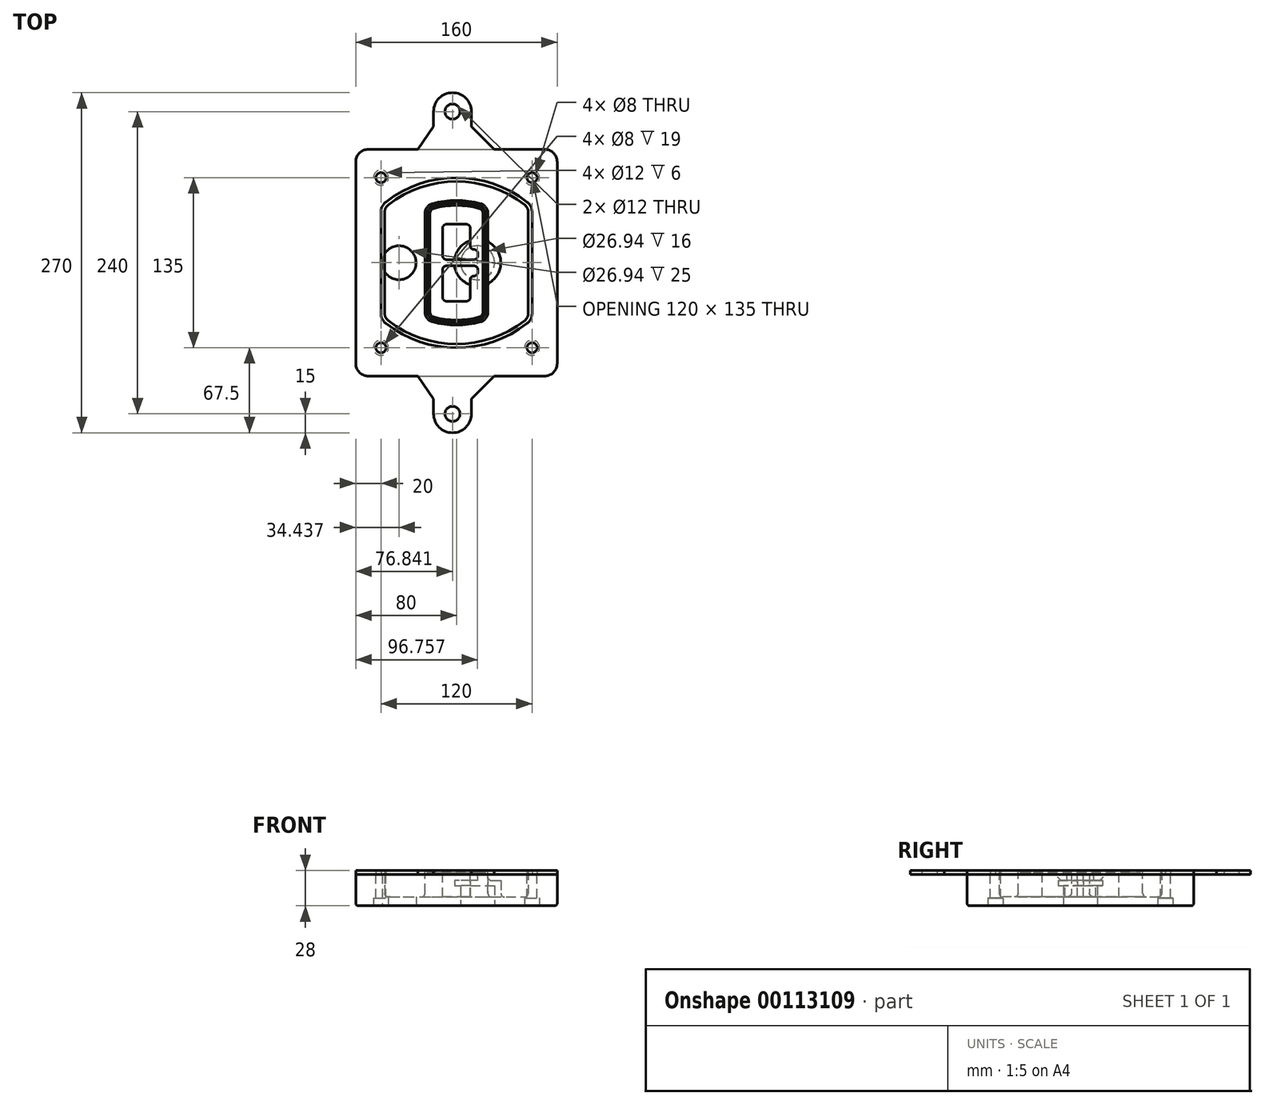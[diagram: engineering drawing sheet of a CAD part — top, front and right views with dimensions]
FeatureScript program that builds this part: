
annotation { "Feature Type Name" : "Feature", "Feature Type Description" : "" }
export const myFeature = defineFeature(function(context is Context, id is Id, definition is map)
    precondition{}
    {
        {
            var Q0;
            Q0=qCreatedBy(makeId("Top.planeOp"),FACE);
            var sketch = newSketch(context, id + "F0", { "sketchPlane" : qUnion([Q0])});
            skPoint(sketch, "E0.rect.middle", {"position": v(0, 0) * mm});
            skLineSegment(sketch, "E1.bottom", {"start": v(-70, -90) * mm, "end": v(70, -90) * mm});
            skLineSegment(sketch, "E1.top", {"start": v(-70, 90) * mm, "end": v(70, 90) * mm});
            skLineSegment(sketch, "E1.left", {"start": v(-80, -80) * mm, "end": v(-80, 80) * mm});
            skLineSegment(sketch, "E1.right", {"start": v(80, -80) * mm, "end": v(80, 80) * mm});
            skLineSegment(sketch, "E2", {"start": v(-80, 90) * mm, "end": v(80, -90) * mm, "construction": true});
            skLineSegment(sketch, "E3", {"start": v(80, 90) * mm, "end": v(-80, -90) * mm, "construction": true});
            skCircle(sketch, "E4", {"center": v(-60, 67.5) * mm, "radius": 4 * mm});
            skCircle(sketch, "E5", {"center": v(60, 67.5) * mm, "radius": 4 * mm});
            skCircle(sketch, "E6", {"center": v(60, -67.5) * mm, "radius": 4 * mm});
            skCircle(sketch, "E7", {"center": v(-60, -67.5) * mm, "radius": 4 * mm});
            skLineSegment(sketch, "E8", {"start": v(-60, 67.5) * mm, "end": v(60, 67.5) * mm, "construction": true});
            skLineSegment(sketch, "E9", {"start": v(60, 67.5) * mm, "end": v(60, -67.5) * mm, "construction": true});
            skLineSegment(sketch, "E10", {"start": v(60, -67.5) * mm, "end": v(-60, -67.5) * mm, "construction": true});
            skLineSegment(sketch, "E11", {"start": v(-60, -67.5) * mm, "end": v(-60, 67.5) * mm, "construction": true});
            skLineSegment(sketch, "E12", {"start": v(-60, 40.3) * mm, "end": v(-60, -40.3) * mm});
            skLineSegment(sketch, "E13", {"start": v(60, 40.3) * mm, "end": v(60, -40.3) * mm});
            skArc(sketch, "E14", {"start": v(56.15, 48.18) * mm, "mid": v(0, 67.5) * mm, "end": v(-56.15, 48.18) * mm});
            skArc(sketch, "E15", {"start": v(-56.15, -48.18) * mm, "mid": v(0, -67.5) * mm, "end": v(56.15, -48.18) * mm});
            skLineSegment(sketch, "E16", {"start": v(-60, 0) * mm, "end": v(60, 0) * mm, "construction": true});
            skPoint(sketch, "E17.visualSharp", {"position": v(-60, -45) * mm});
            skArc(sketch, "E17.filletArc", {"start": v(-60, -40.3) * mm, "mid": v(-58.99, -44.68) * mm, "end": v(-56.15, -48.18) * mm});
            skPoint(sketch, "E18.visualSharp", {"position": v(-60, 45) * mm});
            skArc(sketch, "E18.filletArc", {"start": v(-56.15, 48.18) * mm, "mid": v(-58.99, 44.68) * mm, "end": v(-60, 40.3) * mm});
            skPoint(sketch, "E19.visualSharp", {"position": v(60, 45) * mm});
            skArc(sketch, "E19.filletArc", {"start": v(60, 40.3) * mm, "mid": v(58.99, 44.68) * mm, "end": v(56.15, 48.18) * mm});
            skPoint(sketch, "E20.visualSharp", {"position": v(60, -45) * mm});
            skArc(sketch, "E20.filletArc", {"start": v(56.15, -48.18) * mm, "mid": v(58.99, -44.68) * mm, "end": v(60, -40.3) * mm});
            skPoint(sketch, "E21.visualSharp", {"position": v(-80, 90) * mm});
            skArc(sketch, "E21.filletArc", {"start": v(-70, 90) * mm, "mid": v(-77.07, 87.07) * mm, "end": v(-80, 80) * mm});
            skPoint(sketch, "E22.visualSharp", {"position": v(80, 90) * mm});
            skArc(sketch, "E22.filletArc", {"start": v(80, 80) * mm, "mid": v(77.07, 87.07) * mm, "end": v(70, 90) * mm});
            skPoint(sketch, "E23.visualSharp", {"position": v(80, -90) * mm});
            skArc(sketch, "E23.filletArc", {"start": v(70, -90) * mm, "mid": v(77.07, -87.07) * mm, "end": v(80, -80) * mm});
            skPoint(sketch, "E24.visualSharp", {"position": v(-80, -90) * mm});
            skArc(sketch, "E24.filletArc", {"start": v(-80, -80) * mm, "mid": v(-77.07, -87.07) * mm, "end": v(-70, -90) * mm});
            skArc(sketch, "E25.0", {"start": v(57, 40.3) * mm, "mid": v(56.3, 43.36) * mm, "end": v(54.3, 45.81) * mm});
            skLineSegment(sketch, "E25.1", {"start": v(57, 40.3) * mm, "end": v(57, -40.3) * mm});
            skArc(sketch, "E25.2", {"start": v(54.3, -45.81) * mm, "mid": v(56.3, -43.36) * mm, "end": v(57, -40.3) * mm});
            skArc(sketch, "E25.3", {"start": v(-54.3, -45.81) * mm, "mid": v(0, -64.5) * mm, "end": v(54.3, -45.81) * mm});
            skArc(sketch, "E25.4", {"start": v(-57, -40.3) * mm, "mid": v(-56.3, -43.36) * mm, "end": v(-54.3, -45.81) * mm});
            skArc(sketch, "E25.5", {"start": v(54.3, 45.81) * mm, "mid": v(0, 64.5) * mm, "end": v(-54.3, 45.81) * mm});
            skLineSegment(sketch, "E25.6", {"start": v(-57, 40.3) * mm, "end": v(-57, -40.3) * mm});
            skArc(sketch, "E25.7", {"start": v(-54.3, 45.81) * mm, "mid": v(-56.3, 43.36) * mm, "end": v(-57, 40.3) * mm});
            skArc(sketch, "E26.0", {"start": v(-58.62, 51.33) * mm, "mid": v(-62.58, 46.43) * mm, "end": v(-64, 40.3) * mm});
            skArc(sketch, "E26.1", {"start": v(58.62, 51.33) * mm, "mid": v(0, 71.5) * mm, "end": v(-58.62, 51.33) * mm});
            skArc(sketch, "E26.2", {"start": v(64, 40.3) * mm, "mid": v(62.58, 46.43) * mm, "end": v(58.62, 51.33) * mm});
            skLineSegment(sketch, "E26.3", {"start": v(64, 40.3) * mm, "end": v(64, -40.3) * mm});
            skArc(sketch, "E26.4", {"start": v(58.62, -51.33) * mm, "mid": v(62.58, -46.43) * mm, "end": v(64, -40.3) * mm});
            skLineSegment(sketch, "E26.5", {"start": v(-64, 40.3) * mm, "end": v(-64, -40.3) * mm});
            skArc(sketch, "E26.6", {"start": v(-58.62, -51.33) * mm, "mid": v(0, -71.5) * mm, "end": v(58.62, -51.33) * mm});
            skArc(sketch, "E26.7", {"start": v(-64, -40.3) * mm, "mid": v(-62.58, -46.43) * mm, "end": v(-58.62, -51.33) * mm});
            skSolve(sketch);
        }
        {
            var Q0;
            Q0=makeQuery(id+"F0.imprint","IMPRINT",FACE,{"disambiguationData":[TD([[makeQuery(id+"F0.imprint","IMPRINT",EDGE,{"derivedFrom":sQuery(id+"F0.wireOp",EDGE,"E1.bottom")}),1.0]])]});
            var Q1;
            Q1=makeQuery(id+"F0.imprint","IMPRINT",FACE,{"disambiguationData":[TD([[makeQuery(id+"F0.imprint","IMPRINT",EDGE,{"derivedFrom":sQuery(id+"F0.wireOp",EDGE,"E12")}),1.0]])]});
            var Q2;
            Q2=makeQuery(id+"F0.imprint","IMPRINT",FACE,{"disambiguationData":[TD([[makeQuery(id+"F0.imprint","IMPRINT",EDGE,{"derivedFrom":sQuery(id+"F0.wireOp",EDGE,"E25.0")}),1.0]])]});
            var Q3;
            Q3=makeQuery(id+"F0.imprint","IMPRINT",FACE,{"disambiguationData":[TD([[makeQuery(id+"F0.imprint","IMPRINT",EDGE,{"derivedFrom":sQuery(id+"F0.wireOp",EDGE,"E12")}),-1.0]])]});
            extrude(context, id + "F1", {"entities" : qUnion([Q0, Q1, Q2, Q3]), "oppositeDirection" : true, "depth" : 25 * mm});
        }
        {
            var Q0;
            Q0=makeQuery(id+"F0.imprint","IMPRINT",FACE,{"disambiguationData":[TD([[makeQuery(id+"F0.imprint","IMPRINT",EDGE,{"derivedFrom":sQuery(id+"F0.wireOp",EDGE,"E12")}),1.0]])]});
            extrude(context, id + "F2", {"entities" : qUnion([Q0]), "operationType" : NewBodyOperationType.ADD, "depth" : 3 * mm});
        }
        {
            var Q0;
            Q0=makeQuery(id+"F0.imprint","IMPRINT",FACE,{"disambiguationData":[TD([[makeQuery(id+"F0.imprint","IMPRINT",EDGE,{"derivedFrom":sQuery(id+"F0.wireOp",EDGE,"E25.0")}),1.0]])]});
            extrude(context, id + "F3", {"entities" : qUnion([Q0]), "operationType" : NewBodyOperationType.REMOVE, "oppositeDirection" : true, "depth" : 18 * mm});
        }
        {
            var Q0;
            Q0=makeQuery(id+"F2.opExtrude","CAP_FACE",FACE,{"disambiguationData":[OSD([sQuery(id+"F0.wireOp",EDGE,"E12"),sQuery(id+"F0.wireOp",EDGE,"E13"),sQuery(id+"F0.wireOp",EDGE,"E14"),sQuery(id+"F0.wireOp",EDGE,"E15"),sQuery(id+"F0.wireOp",EDGE,"E17.filletArc"),sQuery(id+"F0.wireOp",EDGE,"E18.filletArc"),sQuery(id+"F0.wireOp",EDGE,"E19.filletArc"),sQuery(id+"F0.wireOp",EDGE,"E20.filletArc"),sQuery(id+"F0.wireOp",EDGE,"E25.0"),sQuery(id+"F0.wireOp",EDGE,"E25.1"),sQuery(id+"F0.wireOp",EDGE,"E25.2"),sQuery(id+"F0.wireOp",EDGE,"E25.3"),sQuery(id+"F0.wireOp",EDGE,"E25.4"),sQuery(id+"F0.wireOp",EDGE,"E25.5"),sQuery(id+"F0.wireOp",EDGE,"E25.6"),sQuery(id+"F0.wireOp",EDGE,"E25.7")])],"isStart":false});
            var sketch = newSketch(context, id + "F4", { "sketchPlane" : qUnion([Q0])});
            skArc(sketch, "E27.0", {"start": v(-19.08, -46.97) * mm, "mid": v(0, -49.5) * mm, "end": v(19.08, -46.97) * mm});
            skArc(sketch, "E28.0", {"start": v(19.08, 46.97) * mm, "mid": v(0, 49.5) * mm, "end": v(-19.08, 46.97) * mm});
            skLineSegment(sketch, "E29", {"start": v(-25, 39.25) * mm, "end": v(-25, -39.25) * mm});
            skLineSegment(sketch, "E30", {"start": v(25, 39.25) * mm, "end": v(25, -39.25) * mm});
            skLineSegment(sketch, "E31", {"start": v(-25, 45.1) * mm, "end": v(25, 45.1) * mm, "construction": true});
            skLineSegment(sketch, "E32", {"start": v(-25, -45.1) * mm, "end": v(25, -45.1) * mm, "construction": true});
            skPoint(sketch, "E33.visualSharp", {"position": v(-25, 45.1) * mm});
            skArc(sketch, "E33.filletArc", {"start": v(-19.08, 46.97) * mm, "mid": v(-23.35, 44.11) * mm, "end": v(-25, 39.25) * mm});
            skPoint(sketch, "E34.visualSharp", {"position": v(25, 45.1) * mm});
            skArc(sketch, "E34.filletArc", {"start": v(25, 39.25) * mm, "mid": v(23.35, 44.11) * mm, "end": v(19.08, 46.97) * mm});
            skPoint(sketch, "E35.visualSharp", {"position": v(25, -45.1) * mm});
            skArc(sketch, "E35.filletArc", {"start": v(19.08, -46.97) * mm, "mid": v(23.35, -44.11) * mm, "end": v(25, -39.25) * mm});
            skPoint(sketch, "E36.visualSharp", {"position": v(-25, -45.1) * mm});
            skArc(sketch, "E36.filletArc", {"start": v(-25, -39.25) * mm, "mid": v(-23.35, -44.11) * mm, "end": v(-19.08, -46.97) * mm});
            skArc(sketch, "E37.0", {"start": v(54.3, 45.81) * mm, "mid": v(0, 64.5) * mm, "end": v(-54.3, 45.81) * mm});
            skArc(sketch, "E37.1", {"start": v(-54.3, 45.81) * mm, "mid": v(-56.3, 43.36) * mm, "end": v(-57, 40.3) * mm});
            skLineSegment(sketch, "E37.2", {"start": v(-57, 40.3) * mm, "end": v(-57, -40.3) * mm});
            skArc(sketch, "E37.3", {"start": v(-57, -40.3) * mm, "mid": v(-56.3, -43.36) * mm, "end": v(-54.3, -45.81) * mm});
            skArc(sketch, "E37.4", {"start": v(-54.3, -45.81) * mm, "mid": v(0, -64.5) * mm, "end": v(54.3, -45.81) * mm});
            skArc(sketch, "E37.5", {"start": v(54.3, -45.81) * mm, "mid": v(56.3, -43.36) * mm, "end": v(57, -40.3) * mm});
            skLineSegment(sketch, "E37.6", {"start": v(57, 40.3) * mm, "end": v(57, -40.3) * mm});
            skArc(sketch, "E37.7", {"start": v(57, 40.3) * mm, "mid": v(56.3, 43.36) * mm, "end": v(54.3, 45.81) * mm});
            skLineSegment(sketch, "E38.0", {"start": v(23, 39.25) * mm, "end": v(23, -39.25) * mm});
            skArc(sketch, "E38.1", {"start": v(18.56, -45.04) * mm, "mid": v(21.76, -42.9) * mm, "end": v(23, -39.25) * mm});
            skArc(sketch, "E38.2", {"start": v(-18.56, -45.04) * mm, "mid": v(0, -47.5) * mm, "end": v(18.56, -45.04) * mm});
            skArc(sketch, "E38.3", {"start": v(-23, -39.25) * mm, "mid": v(-21.76, -42.9) * mm, "end": v(-18.56, -45.04) * mm});
            skLineSegment(sketch, "E38.4", {"start": v(-23, 39.25) * mm, "end": v(-23, -39.25) * mm});
            skArc(sketch, "E38.5", {"start": v(23, 39.25) * mm, "mid": v(21.76, 42.9) * mm, "end": v(18.56, 45.04) * mm});
            skArc(sketch, "E38.6", {"start": v(-18.56, 45.04) * mm, "mid": v(-21.76, 42.9) * mm, "end": v(-23, 39.25) * mm});
            skArc(sketch, "E38.7", {"start": v(18.56, 45.04) * mm, "mid": v(0, 47.5) * mm, "end": v(-18.56, 45.04) * mm});
            skArc(sketch, "E39.0", {"start": v(21, 39.25) * mm, "mid": v(20.18, 41.68) * mm, "end": v(18.04, 43.1) * mm});
            skLineSegment(sketch, "E39.1", {"start": v(21, 39.25) * mm, "end": v(21, -39.25) * mm});
            skArc(sketch, "E39.2", {"start": v(18.04, -43.1) * mm, "mid": v(20.18, -41.68) * mm, "end": v(21, -39.25) * mm});
            skArc(sketch, "E39.3", {"start": v(-18.04, -43.1) * mm, "mid": v(0, -45.5) * mm, "end": v(18.04, -43.1) * mm});
            skArc(sketch, "E39.4", {"start": v(-21, -39.25) * mm, "mid": v(-20.18, -41.68) * mm, "end": v(-18.04, -43.1) * mm});
            skArc(sketch, "E39.5", {"start": v(18.04, 43.1) * mm, "mid": v(0, 45.5) * mm, "end": v(-18.04, 43.1) * mm});
            skLineSegment(sketch, "E39.6", {"start": v(-21, 39.25) * mm, "end": v(-21, -39.25) * mm});
            skArc(sketch, "E39.7", {"start": v(-18.04, 43.1) * mm, "mid": v(-20.18, 41.68) * mm, "end": v(-21, 39.25) * mm});
            skLineSegment(sketch, "E40", {"start": v(-25, 0) * mm, "end": v(25, 0) * mm, "construction": true});
            skLineSegment(sketch, "E41", {"start": v(-11, 5.5) * mm, "end": v(-11, 27.5) * mm});
            skLineSegment(sketch, "E42", {"start": v(-8, 30.5) * mm, "end": v(8, 30.5) * mm});
            skLineSegment(sketch, "E43", {"start": v(11, 27.5) * mm, "end": v(11, 13.5) * mm});
            skLineSegment(sketch, "E44", {"start": v(14, 10.5) * mm, "end": v(14, 10.5) * mm});
            skLineSegment(sketch, "E45", {"start": v(17, 7.5) * mm, "end": v(17, 5.5) * mm});
            skLineSegment(sketch, "E46", {"start": v(14, 2.5) * mm, "end": v(-8, 2.5) * mm});
            skPoint(sketch, "E47.visualSharp", {"position": v(-11, 30.5) * mm});
            skArc(sketch, "E47.filletArc", {"start": v(-8, 30.5) * mm, "mid": v(-10.12, 29.62) * mm, "end": v(-11, 27.5) * mm});
            skPoint(sketch, "E48.visualSharp", {"position": v(11, 30.5) * mm});
            skArc(sketch, "E48.filletArc", {"start": v(11, 27.5) * mm, "mid": v(10.12, 29.62) * mm, "end": v(8, 30.5) * mm});
            skPoint(sketch, "E49.visualSharp", {"position": v(11, 10.5) * mm});
            skArc(sketch, "E49.filletArc", {"start": v(11, 13.5) * mm, "mid": v(11.88, 11.38) * mm, "end": v(14, 10.5) * mm});
            skPoint(sketch, "E50.visualSharp", {"position": v(17, 10.5) * mm});
            skArc(sketch, "E50.filletArc", {"start": v(17, 7.5) * mm, "mid": v(16.12, 9.62) * mm, "end": v(14, 10.5) * mm});
            skPoint(sketch, "E51.visualSharp", {"position": v(17, 2.5) * mm});
            skArc(sketch, "E51.filletArc", {"start": v(14, 2.5) * mm, "mid": v(16.12, 3.38) * mm, "end": v(17, 5.5) * mm});
            skPoint(sketch, "E52.visualSharp", {"position": v(-11, 2.5) * mm});
            skArc(sketch, "E52.filletArc", {"start": v(-11, 5.5) * mm, "mid": v(-10.12, 3.38) * mm, "end": v(-8, 2.5) * mm});
            skLineSegment(sketch, "E53.0.MirrorCS", {"start": v(14, -2.5) * mm, "end": v(-8, -2.5) * mm});
            skArc(sketch, "E54.0.MirrorCS", {"start": v(-11, -5.5) * mm, "mid": v(-10.12, -3.38) * mm, "end": v(-8, -2.5) * mm});
            skLineSegment(sketch, "E55.0.MirrorCS", {"start": v(-11, -5.5) * mm, "end": v(-11, -27.5) * mm});
            skArc(sketch, "E56.0.MirrorCS", {"start": v(-8, -30.5) * mm, "mid": v(-10.12, -29.62) * mm, "end": v(-11, -27.5) * mm});
            skLineSegment(sketch, "E57.0.MirrorCS", {"start": v(-8, -30.5) * mm, "end": v(8, -30.5) * mm});
            skArc(sketch, "E58.0.MirrorCS", {"start": v(11, -27.5) * mm, "mid": v(10.12, -29.62) * mm, "end": v(8, -30.5) * mm});
            skLineSegment(sketch, "E59.0.MirrorCS", {"start": v(11, -27.5) * mm, "end": v(11, -13.5) * mm});
            skArc(sketch, "E60.0.MirrorCS", {"start": v(11, -13.5) * mm, "mid": v(11.88, -11.38) * mm, "end": v(14, -10.5) * mm});
            skArc(sketch, "E61.0.MirrorCS", {"start": v(17, -7.5) * mm, "mid": v(16.12, -9.62) * mm, "end": v(14, -10.5) * mm});
            skLineSegment(sketch, "E62.0.MirrorCS", {"start": v(17, -7.5) * mm, "end": v(17, -5.5) * mm});
            skArc(sketch, "E63.0.MirrorCS", {"start": v(14, -2.5) * mm, "mid": v(16.12, -3.38) * mm, "end": v(17, -5.5) * mm});
            skSolve(sketch);
        }
        {
            var Q0;
            Q0=makeQuery(id+"F4.imprint","IMPRINT",FACE,{"disambiguationData":[TD([[makeQuery(id+"F4.imprint","IMPRINT",EDGE,{"derivedFrom":sQuery(id+"F4.wireOp",EDGE,"E27.0")}),1.0]])]});
            var Q1;
            Q1=makeQuery(id+"F4.imprint","IMPRINT",FACE,{"disambiguationData":[TD([[makeQuery(id+"F4.imprint","IMPRINT",EDGE,{"derivedFrom":sQuery(id+"F4.wireOp",EDGE,"E38.0")}),-1.0]])]});
            var Q2;
            Q2=makeQuery(id+"F4.imprint","IMPRINT",FACE,{"disambiguationData":[TD([[makeQuery(id+"F4.imprint","IMPRINT",EDGE,{"derivedFrom":sQuery(id+"F4.wireOp",EDGE,"E39.0")}),1.0]])]});
            extrude(context, id + "F5", {"entities" : qUnion([Q0, Q1, Q2]), "operationType" : NewBodyOperationType.ADD, "endBound" : BoundingType.UP_TO_NEXT, "oppositeDirection" : true, "depth" : 25 * mm});
        }
        {
            var Q0;
            Q0=makeQuery(id+"F4.imprint","IMPRINT",FACE,{"disambiguationData":[TD([[makeQuery(id+"F4.imprint","IMPRINT",EDGE,{"derivedFrom":sQuery(id+"F4.wireOp",EDGE,"E38.0")}),-1.0]])]});
            extrude(context, id + "F6", {"entities" : qUnion([Q0]), "operationType" : NewBodyOperationType.REMOVE, "oppositeDirection" : true, "depth" : 2 * mm});
        }
        {
            var Q0;
            Q0=makeQuery(id+"F1.opExtrude","CAP_FACE",FACE,{"disambiguationData":[OSD([sQuery(id+"F0.wireOp",EDGE,"E1.bottom"),sQuery(id+"F0.wireOp",EDGE,"E1.top"),sQuery(id+"F0.wireOp",EDGE,"E1.left"),sQuery(id+"F0.wireOp",EDGE,"E1.right"),sQuery(id+"F0.wireOp",EDGE,"E4"),sQuery(id+"F0.wireOp",EDGE,"E5"),sQuery(id+"F0.wireOp",EDGE,"E6"),sQuery(id+"F0.wireOp",EDGE,"E7"),sQuery(id+"F0.wireOp",EDGE,"E21.filletArc"),sQuery(id+"F0.wireOp",EDGE,"E22.filletArc"),sQuery(id+"F0.wireOp",EDGE,"E23.filletArc"),sQuery(id+"F0.wireOp",EDGE,"E24.filletArc")])],"isStart":false});
            var sketch = newSketch(context, id + "F7", { "sketchPlane" : qUnion([Q0])});
            skCircle(sketch, "E64", {"center": v(16.76, 0) * mm, "radius": 13.47 * mm});
            skCircle(sketch, "E65", {"center": v(-45.56, 0) * mm, "radius": 13.47 * mm});
            skLineSegment(sketch, "E66", {"start": v(80, 0) * mm, "end": v(-80, 0) * mm});
            skCircle(sketch, "E67", {"center": v(16.76, 0) * mm, "radius": 18.47 * mm});
            skCircle(sketch, "E68", {"center": v(60, -67.5) * mm, "radius": 6 * mm});
            skCircle(sketch, "E69", {"center": v(-60, -67.5) * mm, "radius": 6 * mm});
            skCircle(sketch, "E70", {"center": v(-60, 67.5) * mm, "radius": 6 * mm});
            skCircle(sketch, "E71", {"center": v(60, 67.5) * mm, "radius": 6 * mm});
            skSolve(sketch);
        }
        {
            var Q0;
            {var subQ1=sQuery(id+"F7.wireOp",EDGE,"E66");var subQ4=sQuery(id+"F7.wireOp",EDGE,"E64");var subQ6=makeQuery(id+"F7.imprint","INTERSECT",VERTEX,{"disambiguationData":[OD(0.0)],"derivedFrom":[subQ4,subQ1]});Q0=makeQuery(id+"F7.imprint","IMPRINT",FACE,{"disambiguationData":[TD([[makeQuery(id+"F7.imprint","IMPRINT",EDGE,{"disambiguationData":[TD([[subQ6,-1.0]])],"derivedFrom":subQ4}),-1.0]])]});}
            var Q1;
            {var subQ0=sQuery(id+"F7.wireOp",EDGE,"E66");var subQ1=sQuery(id+"F7.wireOp",EDGE,"E64");var subQ3=makeQuery(id+"F7.imprint","INTERSECT",VERTEX,{"disambiguationData":[OD(0.0)],"derivedFrom":[subQ1,subQ0]});Q1=makeQuery(id+"F7.imprint","IMPRINT",FACE,{"disambiguationData":[TD([[makeQuery(id+"F7.imprint","IMPRINT",EDGE,{"disambiguationData":[TD([[subQ3,-1.0]])],"derivedFrom":subQ1}),1.0]])]});}
            var Q2;
            {var subQ0=sQuery(id+"F7.wireOp",EDGE,"E66");var subQ1=sQuery(id+"F7.wireOp",EDGE,"E64");var subQ3=makeQuery(id+"F7.imprint","INTERSECT",VERTEX,{"disambiguationData":[OD(0.0)],"derivedFrom":[subQ1,subQ0]});Q2=makeQuery(id+"F7.imprint","IMPRINT",FACE,{"disambiguationData":[TD([[makeQuery(id+"F7.imprint","IMPRINT",EDGE,{"disambiguationData":[TD([[subQ3,1.0]])],"derivedFrom":subQ1}),1.0]])]});}
            var Q3;
            {var subQ1=sQuery(id+"F7.wireOp",EDGE,"E66");var subQ4=sQuery(id+"F7.wireOp",EDGE,"E64");var subQ6=makeQuery(id+"F7.imprint","INTERSECT",VERTEX,{"disambiguationData":[OD(0.0)],"derivedFrom":[subQ4,subQ1]});Q3=makeQuery(id+"F7.imprint","IMPRINT",FACE,{"disambiguationData":[TD([[makeQuery(id+"F7.imprint","IMPRINT",EDGE,{"disambiguationData":[TD([[subQ6,1.0]])],"derivedFrom":subQ4}),-1.0]])]});}
            extrude(context, id + "F8", {"entities" : qUnion([Q0, Q1, Q2, Q3]), "operationType" : NewBodyOperationType.ADD, "oppositeDirection" : true, "depth" : 20 * mm});
        }
        {
            var Q0;
            {var subQ0=sQuery(id+"F7.wireOp",EDGE,"E66");var subQ1=sQuery(id+"F7.wireOp",EDGE,"E64");var subQ3=makeQuery(id+"F7.imprint","INTERSECT",VERTEX,{"disambiguationData":[OD(0.0)],"derivedFrom":[subQ1,subQ0]});Q0=makeQuery(id+"F7.imprint","IMPRINT",FACE,{"disambiguationData":[TD([[makeQuery(id+"F7.imprint","IMPRINT",EDGE,{"disambiguationData":[TD([[subQ3,-1.0]])],"derivedFrom":subQ1}),1.0]])]});}
            var Q1;
            {var subQ0=sQuery(id+"F7.wireOp",EDGE,"E66");var subQ1=sQuery(id+"F7.wireOp",EDGE,"E64");var subQ3=makeQuery(id+"F7.imprint","INTERSECT",VERTEX,{"disambiguationData":[OD(0.0)],"derivedFrom":[subQ1,subQ0]});Q1=makeQuery(id+"F7.imprint","IMPRINT",FACE,{"disambiguationData":[TD([[makeQuery(id+"F7.imprint","IMPRINT",EDGE,{"disambiguationData":[TD([[subQ3,1.0]])],"derivedFrom":subQ1}),1.0]])]});}
            extrude(context, id + "F9", {"entities" : qUnion([Q0, Q1]), "operationType" : NewBodyOperationType.REMOVE, "oppositeDirection" : true, "depth" : 16 * mm});
        }
        {
            var Q0;
            {var subQ0=sQuery(id+"F7.wireOp",EDGE,"E66");var subQ1=sQuery(id+"F7.wireOp",EDGE,"E65");var subQ3=makeQuery(id+"F7.imprint","INTERSECT",VERTEX,{"disambiguationData":[OD(0.0)],"derivedFrom":[subQ1,subQ0]});Q0=makeQuery(id+"F7.imprint","IMPRINT",FACE,{"disambiguationData":[TD([[makeQuery(id+"F7.imprint","IMPRINT",EDGE,{"disambiguationData":[TD([[subQ3,-1.0]])],"derivedFrom":subQ1}),1.0]])]});}
            var Q1;
            {var subQ0=sQuery(id+"F7.wireOp",EDGE,"E66");var subQ1=sQuery(id+"F7.wireOp",EDGE,"E65");var subQ3=makeQuery(id+"F7.imprint","INTERSECT",VERTEX,{"disambiguationData":[OD(0.0)],"derivedFrom":[subQ1,subQ0]});Q1=makeQuery(id+"F7.imprint","IMPRINT",FACE,{"disambiguationData":[TD([[makeQuery(id+"F7.imprint","IMPRINT",EDGE,{"disambiguationData":[TD([[subQ3,1.0]])],"derivedFrom":subQ1}),1.0]])]});}
            extrude(context, id + "F10", {"entities" : qUnion([Q0, Q1]), "operationType" : NewBodyOperationType.REMOVE, "oppositeDirection" : true, "depth" : 25 * mm});
        }
        {
            var Q0;
            {var subQ0=sQuery(id+"F0.wireOp",EDGE,"E22.filletArc");var subQ1=sQuery(id+"F0.wireOp",EDGE,"E7");var subQ2=sQuery(id+"F0.wireOp",EDGE,"E6");var subQ3=sQuery(id+"F0.wireOp",EDGE,"E5");var subQ4=sQuery(id+"F0.wireOp",EDGE,"E4");var subQ5=sQuery(id+"F0.wireOp",EDGE,"E1.bottom");var subQ6=sQuery(id+"F0.wireOp",EDGE,"E21.filletArc");var subQ7=sQuery(id+"F0.wireOp",EDGE,"E1.top");var subQ8=sQuery(id+"F0.wireOp",EDGE,"E1.left");var subQ9=sQuery(id+"F0.wireOp",EDGE,"E1.right");var subQ10=sQuery(id+"F0.wireOp",EDGE,"E23.filletArc");var subQ11=sQuery(id+"F0.wireOp",EDGE,"E24.filletArc");Q0=makeQuery(id+"F2.boolean.opBoolean","SPLIT",FACE,{"disambiguationData":[TD([makeQuery(id+"F1.opExtrude","SWEPT_FACE",FACE,{"disambiguationData":[OSD([subQ5])]})])],"derivedFrom":makeQuery(id+"F1.opExtrude","CAP_FACE",FACE,{"disambiguationData":[OSD([subQ5,subQ7,subQ8,subQ9,subQ4,subQ3,subQ2,subQ1,subQ6,subQ0,subQ10,subQ11])],"isStart":true})});}
            var sketch = newSketch(context, id + "F11", { "sketchPlane" : qUnion([Q0])});
            skLineSegment(sketch, "E72", {"start": v(-30.53, 90) * mm, "end": v(-18.16, 108) * mm});
            skLineSegment(sketch, "E73", {"start": v(-18.16, 108) * mm, "end": v(-18.16, 120) * mm});
            skLineSegment(sketch, "E74", {"start": v(11.84, 108) * mm, "end": v(11.84, 120) * mm});
            skArc(sketch, "E75", {"start": v(11.84, 120) * mm, "mid": v(-3.16, 135) * mm, "end": v(-18.16, 120) * mm});
            skCircle(sketch, "E76", {"center": v(-3.16, 120) * mm, "radius": 6 * mm});
            skLineSegment(sketch, "E77", {"start": v(-3.16, 90) * mm, "end": v(-3.16, 120) * mm, "construction": true});
            skLineSegment(sketch, "E78", {"start": v(11.84, 108) * mm, "end": v(29.84, 90) * mm});
            skLineSegment(sketch, "E79", {"start": v(-80, 0) * mm, "end": v(80, 0) * mm, "construction": true});
            skLineSegment(sketch, "E80.MirrorCS", {"start": v(-30.53, -90) * mm, "end": v(-18.16, -108) * mm});
            skLineSegment(sketch, "E81.MirrorCS", {"start": v(-18.16, -108) * mm, "end": v(-18.16, -120) * mm});
            skArc(sketch, "E82.MirrorCS", {"start": v(11.84, -120) * mm, "mid": v(-3.16, -135) * mm, "end": v(-18.16, -120) * mm});
            skLineSegment(sketch, "E83.MirrorCS", {"start": v(11.84, -108) * mm, "end": v(11.84, -120) * mm});
            skLineSegment(sketch, "E84.MirrorCS", {"start": v(11.84, -108) * mm, "end": v(29.84, -90) * mm});
            skCircle(sketch, "E85.MirrorC", {"center": v(-3.16, -120) * mm, "radius": 6 * mm});
            skLineSegment(sketch, "E86.MirrorCS", {"start": v(-3.16, -90) * mm, "end": v(-3.16, -120) * mm, "construction": true});
            skSolve(sketch);
        }
        {
            var Q0;
            Q0=makeQuery(id+"F7.imprint","IMPRINT",FACE,{"disambiguationData":[TD([[makeQuery(id+"F7.imprint","IMPRINT",EDGE,{"derivedFrom":sQuery(id+"F7.wireOp",EDGE,"E68")}),1.0]])]});
            var Q1;
            Q1=makeQuery(id+"F7.imprint","IMPRINT",FACE,{"disambiguationData":[TD([[makeQuery(id+"F7.imprint","IMPRINT",EDGE,{"derivedFrom":makeQuery(id+"F1.opExtrude","CAP_EDGE",EDGE,{"disambiguationData":[OSD([sQuery(id+"F0.wireOp",EDGE,"E5")])],"isStart":false})}),-1.0]])]});
            var Q2;
            Q2=makeQuery(id+"F7.imprint","IMPRINT",FACE,{"disambiguationData":[TD([[makeQuery(id+"F7.imprint","IMPRINT",EDGE,{"derivedFrom":sQuery(id+"F7.wireOp",EDGE,"E69")}),1.0]])]});
            var Q3;
            Q3=makeQuery(id+"F7.imprint","IMPRINT",FACE,{"disambiguationData":[TD([[makeQuery(id+"F7.imprint","IMPRINT",EDGE,{"derivedFrom":makeQuery(id+"F1.opExtrude","CAP_EDGE",EDGE,{"disambiguationData":[OSD([sQuery(id+"F0.wireOp",EDGE,"E4")])],"isStart":false})}),-1.0]])]});
            var Q4;
            Q4=makeQuery(id+"F7.imprint","IMPRINT",FACE,{"disambiguationData":[TD([[makeQuery(id+"F7.imprint","IMPRINT",EDGE,{"derivedFrom":sQuery(id+"F7.wireOp",EDGE,"E70")}),1.0]])]});
            var Q5;
            Q5=makeQuery(id+"F7.imprint","IMPRINT",FACE,{"disambiguationData":[TD([[makeQuery(id+"F7.imprint","IMPRINT",EDGE,{"derivedFrom":makeQuery(id+"F1.opExtrude","CAP_EDGE",EDGE,{"disambiguationData":[OSD([sQuery(id+"F0.wireOp",EDGE,"E7")])],"isStart":false})}),-1.0]])]});
            var Q6;
            Q6=makeQuery(id+"F7.imprint","IMPRINT",FACE,{"disambiguationData":[TD([[makeQuery(id+"F7.imprint","IMPRINT",EDGE,{"derivedFrom":sQuery(id+"F7.wireOp",EDGE,"E71")}),1.0]])]});
            var Q7;
            Q7=makeQuery(id+"F7.imprint","IMPRINT",FACE,{"disambiguationData":[TD([[makeQuery(id+"F7.imprint","IMPRINT",EDGE,{"derivedFrom":makeQuery(id+"F1.opExtrude","CAP_EDGE",EDGE,{"disambiguationData":[OSD([sQuery(id+"F0.wireOp",EDGE,"E6")])],"isStart":false})}),-1.0]])]});
            extrude(context, id + "F12", {"entities" : qUnion([Q0, Q1, Q2, Q3, Q4, Q5, Q6, Q7]), "operationType" : NewBodyOperationType.REMOVE, "oppositeDirection" : true, "depth" : 6 * mm});
        }
        {
            var Q0;
            Q0=makeQuery(id+"F9.boolean.opBoolean","COPY",FACE,{"derivedFrom":makeQuery(id+"F9.opExtrude","CAP_FACE",FACE,{"disambiguationData":[OSD([sQuery(id+"F7.wireOp",EDGE,"E64")])],"isStart":false})});
            var sketch = newSketch(context, id + "F13", { "sketchPlane" : qUnion([Q0])});
            skArc(sketch, "E87.0", {"start": v(11, 17.55) * mm, "mid": v(2.57, 11.82) * mm, "end": v(-1.54, 2.5) * mm});
            skArc(sketch, "E87.1", {"start": v(-1.54, -2.5) * mm, "mid": v(2.57, -11.82) * mm, "end": v(11, -17.55) * mm});
            skLineSegment(sketch, "E88", {"start": v(-1.54, -2.5) * mm, "end": v(14, -2.5) * mm});
            skLineSegment(sketch, "E89.0", {"start": v(14, 2.5) * mm, "end": v(-1.54, 2.5) * mm});
            skArc(sketch, "E89.1", {"start": v(14, 2.5) * mm, "mid": v(16.12, 3.38) * mm, "end": v(17, 5.5) * mm});
            skLineSegment(sketch, "E89.2", {"start": v(17, 7.5) * mm, "end": v(17, 5.5) * mm});
            skArc(sketch, "E89.3", {"start": v(17, 7.5) * mm, "mid": v(16.12, 9.62) * mm, "end": v(14, 10.5) * mm});
            skArc(sketch, "E89.4", {"start": v(11, 13.5) * mm, "mid": v(11.88, 11.38) * mm, "end": v(14, 10.5) * mm});
            skLineSegment(sketch, "E89.5", {"start": v(11, 17.55) * mm, "end": v(11, 13.5) * mm});
            skLineSegment(sketch, "E89.7", {"start": v(14, -2.5) * mm, "end": v(-1.54, -2.5) * mm});
            skArc(sketch, "E89.8", {"start": v(14, -2.5) * mm, "mid": v(16.12, -3.38) * mm, "end": v(17, -5.5) * mm});
            skLineSegment(sketch, "E89.9", {"start": v(17, -7.5) * mm, "end": v(17, -5.5) * mm});
            skArc(sketch, "E89.10", {"start": v(17, -7.5) * mm, "mid": v(16.12, -9.62) * mm, "end": v(14, -10.5) * mm});
            skArc(sketch, "E89.11", {"start": v(11, -13.5) * mm, "mid": v(11.88, -11.38) * mm, "end": v(14, -10.5) * mm});
            skLineSegment(sketch, "E89.12", {"start": v(11, -17.55) * mm, "end": v(11, -13.5) * mm});
            skPoint(sketch, "E90.orphan", {"position": v(11, -27.5) * mm});
            skPoint(sketch, "E91.orphan", {"position": v(-8, -2.5) * mm});
            skPoint(sketch, "E92.orphan", {"position": v(-8, 2.5) * mm});
            skPoint(sketch, "E93.orphan", {"position": v(11, 27.5) * mm});
            skSolve(sketch);
        }
        {
            var Q0;
            {var subQ7=sQuery(id+"F13.wireOp",EDGE,"E87.0");var subQ14=sQuery(id+"F13.wireOp",EDGE,"E87.1");var subQ16=sQuery(id+"F13.wireOp",EDGE,"E89.1");var subQ18=sQuery(id+"F13.wireOp",EDGE,"E89.8");Q0=qUnion([makeQuery(id+"F13.imprint","IMPRINT",FACE,{"disambiguationData":[TD([[makeQuery(id+"F13.imprint","IMPRINT",EDGE,{"derivedFrom":subQ7}),1.0]])]}),makeQuery(id+"F13.imprint","IMPRINT",FACE,{"disambiguationData":[TD([[makeQuery(id+"F13.imprint","IMPRINT",EDGE,{"derivedFrom":subQ14}),1.0]])]}),makeQuery(id+"F13.imprint","IMPRINT",FACE,{"disambiguationData":[TD([[makeQuery(id+"F13.imprint","IMPRINT",EDGE,{"derivedFrom":subQ16}),1.0]])]}),makeQuery(id+"F13.imprint","IMPRINT",FACE,{"disambiguationData":[TD([[makeQuery(id+"F13.imprint","IMPRINT",EDGE,{"derivedFrom":subQ18}),-1.0]])]})]);}
            var Q1;
            Q1=makeQuery(id+"F5.boolean.opBoolean","SPLIT",FACE,{"disambiguationData":[TD([makeQuery(id+"F5.opExtrude","SWEPT_FACE",FACE,{"disambiguationData":[OSD([sQuery(id+"F4.wireOp",EDGE,"E41")])]})])],"derivedFrom":makeQuery(id+"F3.boolean.opBoolean","COPY",FACE,{"derivedFrom":makeQuery(id+"F3.opExtrude","CAP_FACE",FACE,{"disambiguationData":[OSD([sQuery(id+"F0.wireOp",EDGE,"E25.0"),sQuery(id+"F0.wireOp",EDGE,"E25.1"),sQuery(id+"F0.wireOp",EDGE,"E25.2"),sQuery(id+"F0.wireOp",EDGE,"E25.3"),sQuery(id+"F0.wireOp",EDGE,"E25.4"),sQuery(id+"F0.wireOp",EDGE,"E25.5"),sQuery(id+"F0.wireOp",EDGE,"E25.6"),sQuery(id+"F0.wireOp",EDGE,"E25.7")])],"isStart":false})})});
            extrude(context, id + "F14", {"entities" : qUnion([Q0]), "operationType" : NewBodyOperationType.REMOVE, "endBound" : BoundingType.UP_TO_SURFACE, "endBoundEntityFace" : qUnion([Q1]), "depth" : 25 * mm});
        }
        {
            var Q0;
            Q0=makeQuery(id+"F3.boolean.opBoolean","COPY",EDGE,{"derivedFrom":makeQuery(id+"F3.opExtrude","CAP_EDGE",EDGE,{"disambiguationData":[OSD([sQuery(id+"F0.wireOp",EDGE,"E25.6")])],"isStart":false})});
            var Q1;
            Q1=makeQuery(id+"F8.boolean.opBoolean","INTERSECT",EDGE,{"derivedFrom":[makeQuery(id+"F5.opExtrude","SWEPT_FACE",FACE,{"disambiguationData":[OSD([sQuery(id+"F4.wireOp",EDGE,"E30")])]}),makeQuery(id+"F8.opExtrude","CAP_FACE",FACE,{"disambiguationData":[OSD([sQuery(id+"F7.wireOp",EDGE,"E67")])],"isStart":false})]});
            var Q2;
            Q2=makeQuery(id+"F8.boolean.opBoolean","INTERSECT",EDGE,{"disambiguationData":[OD(1.0)],"derivedFrom":[makeQuery(id+"F5.opExtrude","SWEPT_FACE",FACE,{"disambiguationData":[OSD([sQuery(id+"F4.wireOp",EDGE,"E30")])]}),makeQuery(id+"F8.opExtrude","SWEPT_FACE",FACE,{"disambiguationData":[OSD([sQuery(id+"F7.wireOp",EDGE,"E67")])]})]});
            var Q3;
            {var subQ0=sQuery(id+"F4.wireOp",EDGE,"E30");Q3=makeQuery(id+"F8.boolean.opBoolean","SPLIT",EDGE,{"disambiguationData":[TD([makeQuery(id+"F5.opExtrude","SWEPT_FACE",FACE,{"disambiguationData":[OSD([sQuery(id+"F4.wireOp",EDGE,"E35.filletArc")])]})])],"derivedFrom":makeQuery(id+"F5.opExtrude","CAP_EDGE",EDGE,{"disambiguationData":[OSD([subQ0])],"isStart":false})});}
            var Q4;
            {var subQ0=sQuery(id+"F0.wireOp",EDGE,"E25.7");var subQ1=sQuery(id+"F0.wireOp",EDGE,"E25.1");var subQ2=sQuery(id+"F0.wireOp",EDGE,"E25.6");var subQ3=sQuery(id+"F0.wireOp",EDGE,"E25.5");var subQ4=sQuery(id+"F0.wireOp",EDGE,"E25.4");var subQ5=sQuery(id+"F0.wireOp",EDGE,"E25.0");var subQ6=sQuery(id+"F0.wireOp",EDGE,"E25.2");var subQ7=sQuery(id+"F0.wireOp",EDGE,"E25.3");Q4=makeQuery(id+"F8.boolean.opBoolean","INTERSECT",EDGE,{"derivedFrom":[makeQuery(id+"F5.boolean.opBoolean","SPLIT",FACE,{"disambiguationData":[TD([makeQuery(id+"F2.opExtrude","SWEPT_FACE",FACE,{"disambiguationData":[OSD([subQ5])]})])],"derivedFrom":makeQuery(id+"F3.boolean.opBoolean","COPY",FACE,{"derivedFrom":makeQuery(id+"F3.opExtrude","CAP_FACE",FACE,{"disambiguationData":[OSD([subQ5,subQ1,subQ6,subQ7,subQ4,subQ3,subQ2,subQ0])],"isStart":false})})}),makeQuery(id+"F8.opExtrude","SWEPT_FACE",FACE,{"disambiguationData":[OSD([sQuery(id+"F7.wireOp",EDGE,"E67")])]})]});}
            var Q5;
            Q5=makeQuery(id+"F8.boolean.opBoolean","INTERSECT",EDGE,{"disambiguationData":[OD(0.0)],"derivedFrom":[makeQuery(id+"F5.opExtrude","SWEPT_FACE",FACE,{"disambiguationData":[OSD([sQuery(id+"F4.wireOp",EDGE,"E30")])]}),makeQuery(id+"F8.opExtrude","SWEPT_FACE",FACE,{"disambiguationData":[OSD([sQuery(id+"F7.wireOp",EDGE,"E67")])]})]});
            fillet(context, id + "F15", {"entities" : qUnion([Q0, Q1, Q2, Q3, Q4, Q5]), "radius" : 3 * mm, "tangentPropagation" : true, "allowEdgeOverflow" : false});
        }
        {
            var Q0;
            Q0=makeQuery(id+"F1.opExtrude","CAP_EDGE",EDGE,{"disambiguationData":[OSD([sQuery(id+"F0.wireOp",EDGE,"E1.bottom")])],"isStart":false});
            fillet(context, id + "F16", {"entities" : qUnion([Q0]), "radius" : 2 * mm, "tangentPropagation" : true, "allowEdgeOverflow" : false});
        }
        {
            var Q0;
            Q0=makeQuery(id+"F11.imprint","IMPRINT",FACE,{"disambiguationData":[TD([[makeQuery(id+"F11.imprint","IMPRINT",EDGE,{"derivedFrom":makeQuery(id+"F1.opExtrude","CAP_EDGE",EDGE,{"disambiguationData":[OSD([sQuery(id+"F0.wireOp",EDGE,"E1.left")])],"isStart":true})}),-1.0]])]});
            var Q1;
            {var subQ0=sQuery(id+"F11.wireOp",EDGE,"E72");Q1=makeQuery(id+"F11.imprint","IMPRINT",FACE,{"disambiguationData":[TD([[makeQuery(id+"F11.imprint","IMPRINT",EDGE,{"derivedFrom":subQ0}),-1.0]])]});}
            var Q2;
            {var subQ0=sQuery(id+"F11.wireOp",EDGE,"E80.MirrorCS");Q2=makeQuery(id+"F11.imprint","IMPRINT",FACE,{"disambiguationData":[TD([[makeQuery(id+"F11.imprint","IMPRINT",EDGE,{"derivedFrom":subQ0}),1.0]])]});}
            var Q3;
            Q3=makeQuery(id+"F2.opExtrude","CAP_FACE",FACE,{"disambiguationData":[OSD([sQuery(id+"F0.wireOp",EDGE,"E12"),sQuery(id+"F0.wireOp",EDGE,"E13"),sQuery(id+"F0.wireOp",EDGE,"E14"),sQuery(id+"F0.wireOp",EDGE,"E15"),sQuery(id+"F0.wireOp",EDGE,"E17.filletArc"),sQuery(id+"F0.wireOp",EDGE,"E18.filletArc"),sQuery(id+"F0.wireOp",EDGE,"E19.filletArc"),sQuery(id+"F0.wireOp",EDGE,"E20.filletArc"),sQuery(id+"F0.wireOp",EDGE,"E25.0"),sQuery(id+"F0.wireOp",EDGE,"E25.1"),sQuery(id+"F0.wireOp",EDGE,"E25.2"),sQuery(id+"F0.wireOp",EDGE,"E25.3"),sQuery(id+"F0.wireOp",EDGE,"E25.4"),sQuery(id+"F0.wireOp",EDGE,"E25.5"),sQuery(id+"F0.wireOp",EDGE,"E25.6"),sQuery(id+"F0.wireOp",EDGE,"E25.7")])],"isStart":false});
            extrude(context, id + "F17", {"entities" : qUnion([Q0, Q1, Q2]), "endBound" : BoundingType.UP_TO_SURFACE, "endBoundEntityFace" : qUnion([Q3]), "depth" : 25 * mm});
        }
    });
